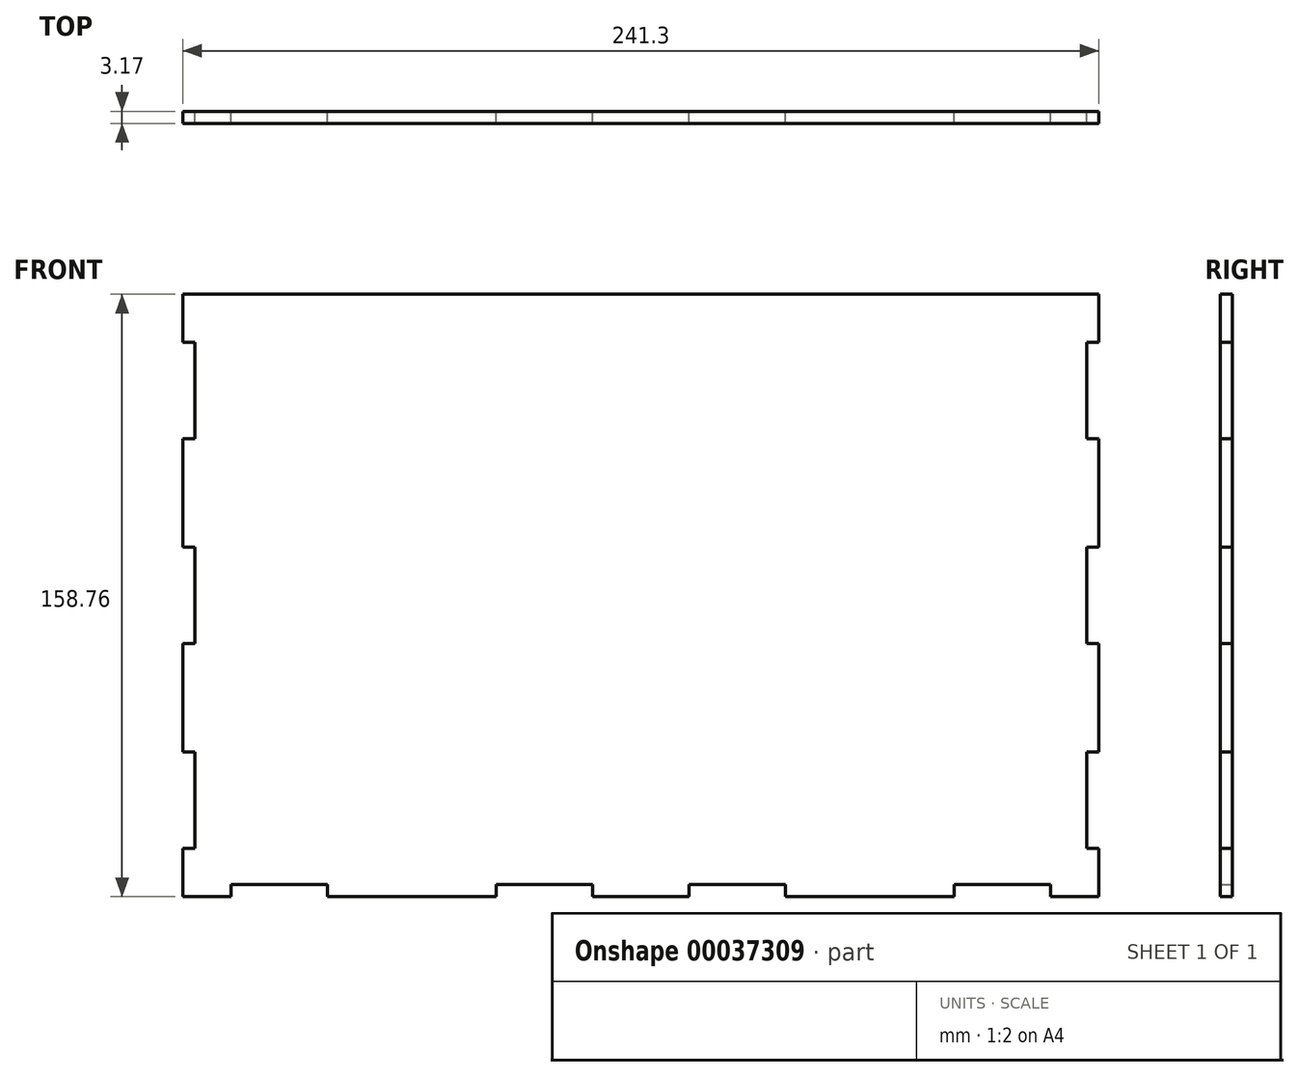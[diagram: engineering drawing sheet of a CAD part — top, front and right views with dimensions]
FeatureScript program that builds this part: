
annotation { "Feature Type Name" : "Feature", "Feature Type Description" : "" }
export const myFeature = defineFeature(function(context is Context, id is Id, definition is map)
    precondition{}
    {
        {
            var Q0;
            Q0=qCreatedBy(makeId("Front.planeOp"),FACE);
            var sketch = newSketch(context, id + "F0", { "sketchPlane" : qUnion([Q0])});
            skLineSegment(sketch, "E0.rect.bottom", {"start": v(120.65, -79.38) * mm, "end": v(-120.65, -79.38) * mm});
            skLineSegment(sketch, "E0.rect.top", {"start": v(120.65, 79.38) * mm, "end": v(-120.65, 79.38) * mm});
            skLineSegment(sketch, "E0.rect.left", {"start": v(120.65, -79.38) * mm, "end": v(120.65, 79.38) * mm});
            skLineSegment(sketch, "E0.rect.right", {"start": v(-120.65, -79.38) * mm, "end": v(-120.65, 79.38) * mm});
            skPoint(sketch, "E0.rect.middle", {"position": v(0, 0) * mm});
            skLineSegment(sketch, "E1", {"start": v(-120.65, 66.68) * mm, "end": v(-117.47, 66.68) * mm});
            skLineSegment(sketch, "E2", {"start": v(-117.48, 66.68) * mm, "end": v(-117.48, 41.28) * mm});
            skLineSegment(sketch, "E3", {"start": v(-117.47, 41.28) * mm, "end": v(-120.65, 41.28) * mm});
            skLineSegment(sketch, "E4", {"start": v(-120.65, -66.68) * mm, "end": v(-117.48, -66.68) * mm});
            skLineSegment(sketch, "E5", {"start": v(-117.48, -66.68) * mm, "end": v(-117.48, -41.28) * mm});
            skLineSegment(sketch, "E6", {"start": v(-117.48, -41.28) * mm, "end": v(-120.65, -41.28) * mm});
            skLineSegment(sketch, "E7", {"start": v(-117.48, 41.28) * mm, "end": v(-117.48, -41.28) * mm, "construction": true});
            skLineSegment(sketch, "E8", {"start": v(-117.48, 0) * mm, "end": v(-117.48, -12.7) * mm});
            skLineSegment(sketch, "E9", {"start": v(-117.48, -12.7) * mm, "end": v(-120.65, -12.7) * mm});
            skLineSegment(sketch, "E10", {"start": v(-117.48, 0) * mm, "end": v(-117.48, 12.7) * mm});
            skLineSegment(sketch, "E11", {"start": v(-117.48, 12.7) * mm, "end": v(-120.65, 12.7) * mm});
            skLineSegment(sketch, "E12", {"start": v(0, 79.38) * mm, "end": v(0, -79.38) * mm, "construction": true});
            skLineSegment(sketch, "E13.MirrorCS", {"start": v(117.47, 66.68) * mm, "end": v(117.47, 41.28) * mm});
            skLineSegment(sketch, "E14.MirrorCS", {"start": v(120.65, 66.68) * mm, "end": v(117.47, 66.68) * mm});
            skLineSegment(sketch, "E15.MirrorCS", {"start": v(117.47, 41.28) * mm, "end": v(120.65, 41.28) * mm});
            skLineSegment(sketch, "E16.MirrorCS", {"start": v(117.48, 12.7) * mm, "end": v(120.65, 12.7) * mm});
            skLineSegment(sketch, "E17.MirrorCS", {"start": v(117.48, 0) * mm, "end": v(117.48, 12.7) * mm});
            skLineSegment(sketch, "E18.MirrorCS", {"start": v(117.48, 0) * mm, "end": v(117.48, -12.7) * mm});
            skLineSegment(sketch, "E19.MirrorCS", {"start": v(117.48, -12.7) * mm, "end": v(120.65, -12.7) * mm});
            skLineSegment(sketch, "E20.MirrorCS", {"start": v(117.48, -41.27) * mm, "end": v(120.65, -41.27) * mm});
            skLineSegment(sketch, "E21.MirrorCS", {"start": v(120.65, -66.67) * mm, "end": v(117.48, -66.67) * mm});
            skLineSegment(sketch, "E22.MirrorCS", {"start": v(117.48, -66.67) * mm, "end": v(117.48, -41.27) * mm});
            skLineSegment(sketch, "E23", {"start": v(-107.95, -79.38) * mm, "end": v(-107.95, -76.2) * mm});
            skLineSegment(sketch, "E24", {"start": v(-107.95, -76.2) * mm, "end": v(-82.55, -76.2) * mm, "construction": true});
            skLineSegment(sketch, "E25", {"start": v(-82.55, -76.2) * mm, "end": v(-82.55, -79.38) * mm});
            skLineSegment(sketch, "E26", {"start": v(-12.7, -76.2) * mm, "end": v(-12.7, -79.38) * mm});
            skLineSegment(sketch, "E27", {"start": v(-38.1, -76.2) * mm, "end": v(-38.1, -79.38) * mm});
            skLineSegment(sketch, "E28", {"start": v(-107.95, -76.2) * mm, "end": v(-82.55, -76.2) * mm});
            skLineSegment(sketch, "E29", {"start": v(-12.7, -76.2) * mm, "end": v(-38.1, -76.2) * mm});
            skLineSegment(sketch, "E30.MirrorCS", {"start": v(12.7, -76.2) * mm, "end": v(38.1, -76.2) * mm});
            skLineSegment(sketch, "E31.MirrorCS", {"start": v(12.7, -76.2) * mm, "end": v(12.7, -79.38) * mm});
            skLineSegment(sketch, "E32.MirrorCS", {"start": v(38.1, -76.2) * mm, "end": v(38.1, -79.38) * mm});
            skLineSegment(sketch, "E33.MirrorCS", {"start": v(107.95, -76.2) * mm, "end": v(82.55, -76.2) * mm});
            skLineSegment(sketch, "E34.MirrorCS", {"start": v(107.95, -79.37) * mm, "end": v(107.95, -76.2) * mm});
            skLineSegment(sketch, "E35.MirrorCS", {"start": v(82.55, -76.2) * mm, "end": v(82.55, -79.37) * mm});
            skSolve(sketch);
        }
        {
            var Q0;
            Q0=makeQuery(id+"F0.imprint","IMPRINT",FACE,{"disambiguationData":[TD([[makeQuery(id+"F0.imprint","IMPRINT",EDGE,{"derivedFrom":sQuery(id+"F0.wireOp",EDGE,"E0.rect.bottom")}),-1.0]])]});
            extrude(context, id + "F1", {"entities" : qUnion([Q0]), "depth" : 3.17 * mm});
        }
    });
